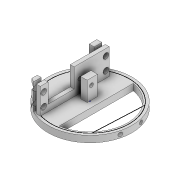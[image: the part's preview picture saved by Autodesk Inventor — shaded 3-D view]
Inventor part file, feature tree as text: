
AUTODESK INVENTOR PART (.ipt)
format: ipt  version: 2021 (Build 250183000, 183)  size: 286,720 bytes
history: native  units: mm
features: sketch x11, extrude x10, other x1
ambient origin geometry x8: Origin, YZ Plane, XZ Plane, XY Plane, X Axis, Y Axis, Z Axis, Center Point
bodies: Body1 (feature_tree)
feature tree (22):
  other  "Sólido1"
  extrude  "Extrusión1"  Depth=65.0mm
  extrude  "Extrusión2"  Depth=16.6mm
  extrude  "Extrusión3"  Depth=9.2mm
  extrude  "Extrusión4"  Depth=53.4mm
  extrude  "Extrusión5"  Depth=30.0mm TaperAngle=0.0deg
  extrude  "Extrusión6"  Depth=5.05mm
  extrude  "Extrusión7"  Depth=2.6mm
  extrude  "Extrusión8"  Depth=4.4mm
  sketch  "Boceto11"  dims[d26=4.4mm d27=4.4mm]
  extrude  "Extrusión9"  Depth=4.4mm
  extrude  "Extrusión10"  Depth=16.6mm
  sketch  "Boceto1"  dims[d1=5.0mm d2=0.0mm d8=65.0mm]
  sketch  "Boceto3"  dims[d9=7.5mm d10=16.6mm]
  sketch  "Boceto4"  dims[d11=53.44mm d12=9.2mm]
  sketch  "Boceto5"  dims[d14=53.4mm d15=53.4mm]
  sketch  "Boceto6"  dims[d16=3.0mm d17=30.0mm d18=0.0mm]
  sketch  "Boceto7"  dims[d19=5.05mm d20=5.05mm]
  sketch  "Boceto8"  dims[d22=2.6mm d23=2.6mm]
  sketch  "Boceto10"  dims[d24=9.9mm d25=4.4mm]
  sketch  "Boceto12"  dims[d28=4.4mm d29=16.6mm]
  sketch  "Boceto13"  dims[d30=13.5mm d31=3.0mm d32=6.0mm d33=6.0mm d34=9.9mm d35=0.0mm d36=2.6mm d37=2.0mm d38=2.0mm d39=20.0mm d40=0.0mm d41=9.9mm d42=4.4mm d43=4.4mm d44=20.0mm d45=6.0mm d46=6.0mm d47=30.0mm d48=0.0mm d54=5.0mm d55=0.0mm d57=4.0mm d58=5.0mm d60=16.6mm d61=7.5mm d62=7.5mm d63=30.1mm d64=0.5mm d65=10.0mm d66=3.0mm d67=0.5mm d68=5.5mm d69=6.0mm d70=1.0mm d71=15.0mm d72=0.0mm d73=1.0mm d74=20.0mm d75=0.0mm d76=22.5mm d77=22.5mm d78=45.0mm d79=45.0mm d80=45.0mm d81=20.0mm d82=0.0mm d83=8.0mm d84=16.0mm d85=3.0mm d86=3.0mm d87=40.0mm d88=0.0mm]
